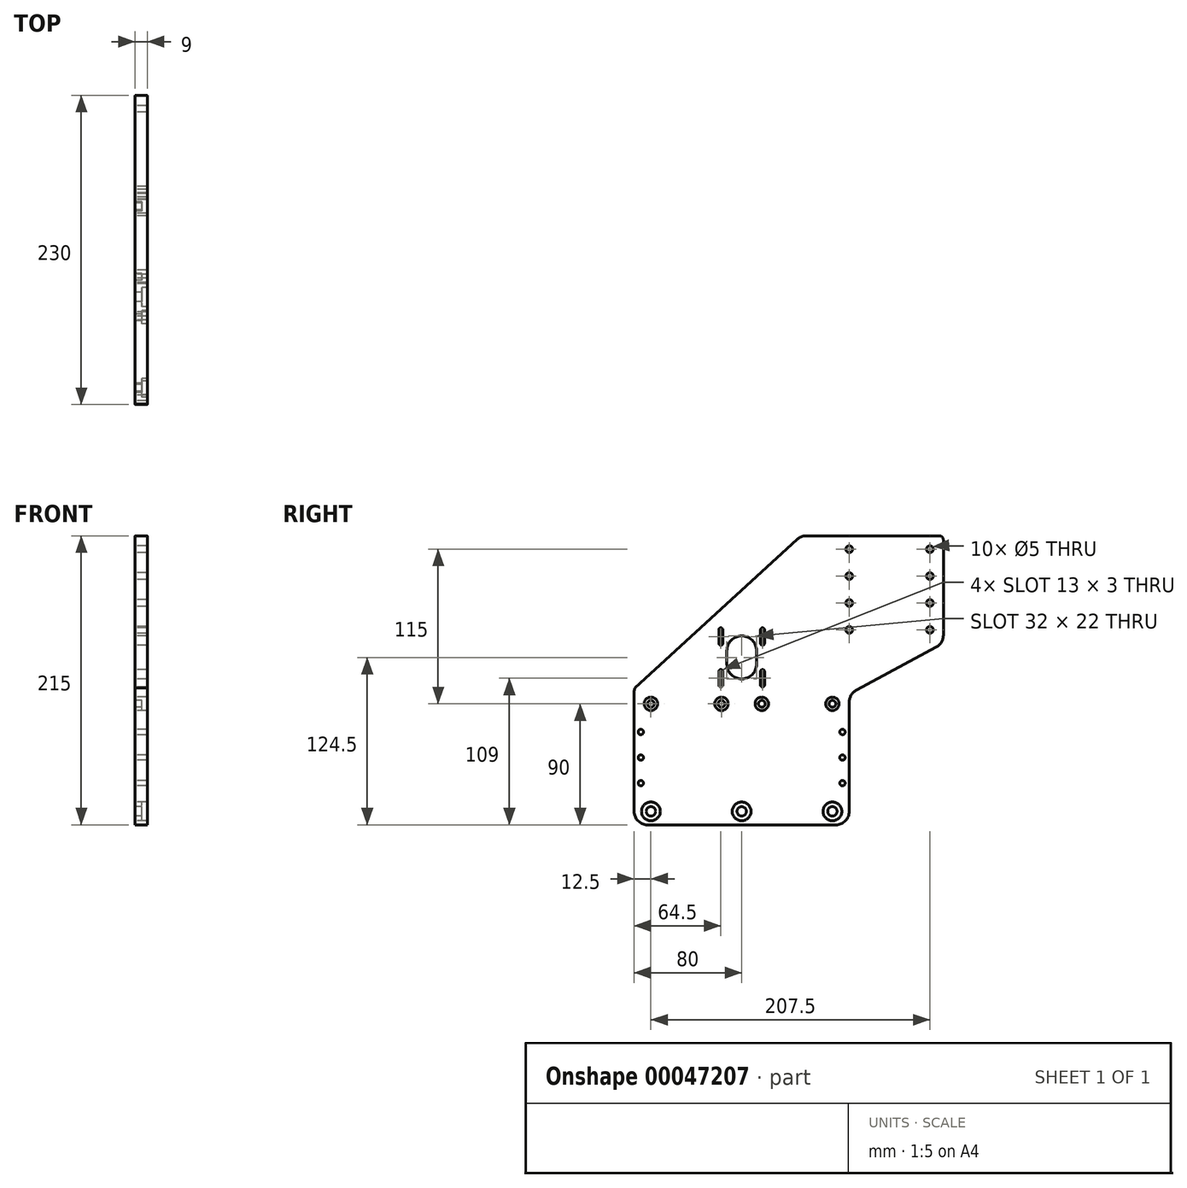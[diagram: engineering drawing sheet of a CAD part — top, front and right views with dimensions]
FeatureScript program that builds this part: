
annotation { "Feature Type Name" : "Feature", "Feature Type Description" : "" }
export const myFeature = defineFeature(function(context is Context, id is Id, definition is map)
    precondition{}
    {
        {
            var Q0;
            Q0=qCreatedBy(makeId("Right.planeOp"),FACE);
            var sketch = newSketch(context, id + "F0", { "sketchPlane" : qUnion([Q0])});
            skLineSegment(sketch, "E0.top", {"start": v(-70, 0) * mm, "end": v(70, 0) * mm});
            skLineSegment(sketch, "E0.left", {"start": v(-80, 98.22) * mm, "end": v(-80, 10) * mm});
            skCircle(sketch, "E1", {"center": v(-67.5, 10) * mm, "radius": 3.5 * mm});
            skCircle(sketch, "E2.MirrorC", {"center": v(67.5, 10) * mm, "radius": 3.5 * mm});
            skCircle(sketch, "E3", {"center": v(-67.5, 90) * mm, "radius": 2.5 * mm});
            skCircle(sketch, "E4.MirrorC", {"center": v(67.5, 90) * mm, "radius": 2.5 * mm});
            skCircle(sketch, "E5", {"center": v(-15, 90) * mm, "radius": 2.5 * mm});
            skCircle(sketch, "E6.MirrorC", {"center": v(15, 90) * mm, "radius": 2.5 * mm});
            skArc(sketch, "E7", {"start": v(-14, 145) * mm, "mid": v(-15.5, 146.5) * mm, "end": v(-17, 145) * mm});
            skArc(sketch, "E8", {"start": v(-17, 135) * mm, "mid": v(-15.5, 133.5) * mm, "end": v(-14, 135) * mm});
            skLineSegment(sketch, "E9", {"start": v(-17, 145) * mm, "end": v(-17, 135) * mm});
            skArc(sketch, "E10", {"start": v(-17, 104) * mm, "mid": v(-15.5, 102.5) * mm, "end": v(-14, 104) * mm});
            skArc(sketch, "E11", {"start": v(-14, 114) * mm, "mid": v(-15.5, 115.5) * mm, "end": v(-17, 114) * mm});
            skLineSegment(sketch, "E12", {"start": v(-17, 114) * mm, "end": v(-17, 104) * mm});
            skLineSegment(sketch, "E13", {"start": v(-15.5, 114) * mm, "end": v(-15.5, 104) * mm, "construction": true});
            skLineSegment(sketch, "E14.MirrorCS", {"start": v(-14, 114) * mm, "end": v(-14, 104) * mm});
            skArc(sketch, "E15.MirrorCS", {"start": v(-14, 104) * mm, "mid": v(-15.5, 102.5) * mm, "end": v(-17, 104) * mm});
            skArc(sketch, "E16.MirrorCS", {"start": v(-17, 114) * mm, "mid": v(-15.5, 115.5) * mm, "end": v(-14, 114) * mm});
            skArc(sketch, "E17.MirrorCS", {"start": v(17, 104) * mm, "mid": v(15.5, 102.5) * mm, "end": v(14, 104) * mm});
            skLineSegment(sketch, "E18.MirrorCS", {"start": v(17, 114) * mm, "end": v(17, 104) * mm});
            skArc(sketch, "E19.MirrorCS", {"start": v(14, 114) * mm, "mid": v(15.5, 115.5) * mm, "end": v(17, 114) * mm});
            skLineSegment(sketch, "E20.MirrorCS", {"start": v(14, 114) * mm, "end": v(14, 104) * mm});
            skArc(sketch, "E21.MirrorCS", {"start": v(17, 114) * mm, "mid": v(15.5, 115.5) * mm, "end": v(14, 114) * mm});
            skLineSegment(sketch, "E22.MirrorCS", {"start": v(15.5, 114) * mm, "end": v(15.5, 104) * mm, "construction": true});
            skArc(sketch, "E23.MirrorCS", {"start": v(14, 104) * mm, "mid": v(15.5, 102.5) * mm, "end": v(17, 104) * mm});
            skLineSegment(sketch, "E24", {"start": v(-15.5, 145) * mm, "end": v(-15.5, 135) * mm, "construction": true});
            skLineSegment(sketch, "E25.MirrorCS", {"start": v(-14, 145) * mm, "end": v(-14, 135) * mm});
            skLineSegment(sketch, "E26.MirrorCS", {"start": v(14, 145) * mm, "end": v(14, 135) * mm});
            skLineSegment(sketch, "E27.MirrorCS", {"start": v(17, 145) * mm, "end": v(17, 135) * mm});
            skLineSegment(sketch, "E28.MirrorCS", {"start": v(15.5, 145) * mm, "end": v(15.5, 135) * mm, "construction": true});
            skArc(sketch, "E29.MirrorCS", {"start": v(17, 135) * mm, "mid": v(15.5, 133.5) * mm, "end": v(14, 135) * mm});
            skArc(sketch, "E30.MirrorCS", {"start": v(14, 145) * mm, "mid": v(15.5, 146.5) * mm, "end": v(17, 145) * mm});
            skLineSegment(sketch, "E31.MirrorCS", {"start": v(80, 91.34) * mm, "end": v(80, 10) * mm});
            skPoint(sketch, "E32.visualSharp", {"position": v(-80, 0) * mm});
            skArc(sketch, "E32.filletArc", {"start": v(-80, 10) * mm, "mid": v(-77.07, 2.93) * mm, "end": v(-70, 0) * mm});
            skPoint(sketch, "E33.visualSharp", {"position": v(80, 0) * mm});
            skArc(sketch, "E33.filletArc", {"start": v(70, 0) * mm, "mid": v(77.07, 2.93) * mm, "end": v(80, 10) * mm});
            skCircle(sketch, "E34", {"center": v(0, 10) * mm, "radius": 3.5 * mm});
            skPoint(sketch, "E35.visualSharp", {"position": v(-80, 100) * mm});
            skArc(sketch, "E35.filletArc", {"start": v(-79.39, 101.67) * mm, "mid": v(-79.85, 99.97) * mm, "end": v(-80, 98.22) * mm});
            skArc(sketch, "E36", {"start": v(11, 129.5) * mm, "mid": v(0, 140.5) * mm, "end": v(-11, 129.5) * mm});
            skArc(sketch, "E37", {"start": v(-11, 119.5) * mm, "mid": v(0, 108.5) * mm, "end": v(11, 119.5) * mm});
            skLineSegment(sketch, "E38", {"start": v(-11, 129.5) * mm, "end": v(-11, 119.5) * mm});
            skLineSegment(sketch, "E39", {"start": v(11, 129.5) * mm, "end": v(11, 119.5) * mm});
            skCircle(sketch, "E40", {"center": v(-75, 69) * mm, "radius": 2 * mm});
            skCircle(sketch, "E41", {"center": v(-75, 50) * mm, "radius": 2 * mm});
            skCircle(sketch, "E42", {"center": v(-75, 31) * mm, "radius": 2 * mm});
            skCircle(sketch, "E43.MirrorC", {"center": v(75, 31) * mm, "radius": 2 * mm});
            skCircle(sketch, "E44.MirrorC", {"center": v(75, 50) * mm, "radius": 2 * mm});
            skCircle(sketch, "E45.MirrorC", {"center": v(75, 69) * mm, "radius": 2 * mm});
            skLineSegment(sketch, "E46", {"start": v(85.26, 100.15) * mm, "end": v(144.74, 132.17) * mm});
            skCircle(sketch, "E47", {"center": v(140, 205) * mm, "radius": 2.5 * mm});
            skCircle(sketch, "E48.0.1.0", {"center": v(140, 185) * mm, "radius": 2.5 * mm});
            skCircle(sketch, "E48.0.2.0", {"center": v(140, 165) * mm, "radius": 2.5 * mm});
            skCircle(sketch, "E48.1.0.0", {"center": v(80, 205) * mm, "radius": 2.5 * mm});
            skCircle(sketch, "E48.1.1.0", {"center": v(80, 185) * mm, "radius": 2.5 * mm});
            skCircle(sketch, "E48.1.2.0", {"center": v(80, 165) * mm, "radius": 2.5 * mm});
            skLineSegment(sketch, "E48.direction1", {"start": v(140, 205) * mm, "end": v(80, 205) * mm, "construction": true});
            skLineSegment(sketch, "E48.direction2", {"start": v(140, 205) * mm, "end": v(140, 185) * mm, "construction": true});
            skPoint(sketch, "E49.visualSharp", {"position": v(150, 215) * mm});
            skPoint(sketch, "E50.visualSharp", {"position": v(150, 135) * mm});
            skArc(sketch, "E50.filletArc", {"start": v(144.74, 132.17) * mm, "mid": v(148.58, 135.85) * mm, "end": v(150, 140.97) * mm});
            skPoint(sketch, "E51.visualSharp", {"position": v(80, 97.32) * mm});
            skArc(sketch, "E51.filletArc", {"start": v(85.26, 100.15) * mm, "mid": v(81.42, 96.47) * mm, "end": v(80, 91.34) * mm});
            skCircle(sketch, "E52.0.0.3", {"center": v(140, 145) * mm, "radius": 2.5 * mm});
            skCircle(sketch, "E52.0.1.3", {"center": v(80, 145) * mm, "radius": 2.5 * mm});
            skLineSegment(sketch, "E53", {"start": v(150, 140.97) * mm, "end": v(150, 212) * mm});
            skLineSegment(sketch, "E54", {"start": v(147, 215) * mm, "end": v(69.19, 215) * mm});
            skLineSegment(sketch, "E55", {"start": v(-79.39, 101.67) * mm, "end": v(41.36, 212.37) * mm});
            skLineSegment(sketch, "E56", {"start": v(48.12, 215) * mm, "end": v(69.19, 215) * mm});
            skPoint(sketch, "E57.visualSharp", {"position": v(44.23, 215) * mm});
            skArc(sketch, "E57.filletArc", {"start": v(48.12, 215) * mm, "mid": v(44.5, 214.32) * mm, "end": v(41.36, 212.37) * mm});
            skArc(sketch, "E58.filletArc", {"start": v(150, 212) * mm, "mid": v(149.12, 214.12) * mm, "end": v(147, 215) * mm});
            skCircle(sketch, "E59", {"center": v(-67.5, 90) * mm, "radius": 5 * mm});
            skCircle(sketch, "E60", {"center": v(-15, 90) * mm, "radius": 5 * mm});
            skCircle(sketch, "E61.MirrorC", {"center": v(15, 90) * mm, "radius": 5 * mm});
            skCircle(sketch, "E62.MirrorC", {"center": v(67.5, 90) * mm, "radius": 5 * mm});
            skCircle(sketch, "E63", {"center": v(-67.5, 10) * mm, "radius": 7 * mm});
            skCircle(sketch, "E64", {"center": v(0, 10) * mm, "radius": 7 * mm});
            skCircle(sketch, "E65.MirrorC", {"center": v(67.5, 10) * mm, "radius": 7 * mm});
            skSolve(sketch);
        }
        {
            var Q0;
            Q0=makeQuery(id+"F0.imprint","IMPRINT",FACE,{"disambiguationData":[TD([[makeQuery(id+"F0.imprint","IMPRINT",EDGE,{"derivedFrom":sQuery(id+"F0.wireOp",EDGE,"E0.top")}),1.0]])]});
            extrude(context, id + "F1", {"entities" : qUnion([Q0]), "depth" : 9 * mm});
        }
        {
            var Q0;
            Q0=makeQuery(id+"F0.imprint","IMPRINT",FACE,{"disambiguationData":[TD([[makeQuery(id+"F0.imprint","IMPRINT",EDGE,{"derivedFrom":sQuery(id+"F0.wireOp",EDGE,"E3")}),-1.0]])]});
            var Q1;
            Q1=makeQuery(id+"F0.imprint","IMPRINT",FACE,{"disambiguationData":[TD([[makeQuery(id+"F0.imprint","IMPRINT",EDGE,{"derivedFrom":sQuery(id+"F0.wireOp",EDGE,"E5")}),-1.0]])]});
            var Q2;
            Q2=makeQuery(id+"F0.imprint","IMPRINT",FACE,{"disambiguationData":[TD([[makeQuery(id+"F0.imprint","IMPRINT",EDGE,{"derivedFrom":sQuery(id+"F0.wireOp",EDGE,"E6.MirrorC")}),1.0]])]});
            var Q3;
            Q3=makeQuery(id+"F0.imprint","IMPRINT",FACE,{"disambiguationData":[TD([[makeQuery(id+"F0.imprint","IMPRINT",EDGE,{"derivedFrom":sQuery(id+"F0.wireOp",EDGE,"E4.MirrorC")}),1.0]])]});
            var Q4;
            Q4=makeQuery(id+"F0.imprint","IMPRINT",FACE,{"disambiguationData":[TD([[makeQuery(id+"F0.imprint","IMPRINT",EDGE,{"derivedFrom":sQuery(id+"F0.wireOp",EDGE,"E2.MirrorC")}),1.0]])]});
            var Q5;
            Q5=makeQuery(id+"F0.imprint","IMPRINT",FACE,{"disambiguationData":[TD([[makeQuery(id+"F0.imprint","IMPRINT",EDGE,{"derivedFrom":sQuery(id+"F0.wireOp",EDGE,"E34")}),-1.0]])]});
            var Q6;
            Q6=makeQuery(id+"F0.imprint","IMPRINT",FACE,{"disambiguationData":[TD([[makeQuery(id+"F0.imprint","IMPRINT",EDGE,{"derivedFrom":sQuery(id+"F0.wireOp",EDGE,"E1")}),-1.0]])]});
            extrude(context, id + "F2", {"entities" : qUnion([Q0, Q1, Q2, Q3, Q4, Q5, Q6]), "operationType" : NewBodyOperationType.ADD, "depth" : 5 * mm});
        }
    });
